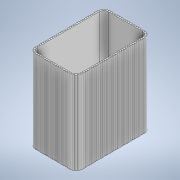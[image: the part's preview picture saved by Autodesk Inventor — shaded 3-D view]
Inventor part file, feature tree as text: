
AUTODESK INVENTOR PART (.ipt)
format: ipt  version: 2020 (Build 240168000, 168)  size: 335,360 bytes
history: native  units: mm
features: extrude x2, sketch x2
ambient origin geometry x8: Origin, YZ Plane, XZ Plane, XY Plane, X Axis, Y Axis, Z Axis, Center Point
bodies: Body1 (feature_tree)
feature tree (4):
  extrude  "Extrusion3"  Depth=10.0mm
  extrude  "Extrusion4"  Depth=10.0mm
  sketch  "Sketch3"  dims[d50=10.0mm d51=10.0mm]
  sketch  "Sketch4"  dims[d52=10.0mm d53=10.0mm d66=113.882734mm d67=360.0deg d68=22.5deg d69=50.0mm d71=90.0deg d73=290.0mm d75=22.5deg d76=20.0mm d78=82.831853mm d81=20.0mm d83=133.882734mm d84=160.0mm d86=22.5deg d89=152.4mm d90=0.0mm d94=20.0mm d98=360.0deg d99=113.882734mm d100=1.2mm d101=149.4mm d102=0.0mm]
